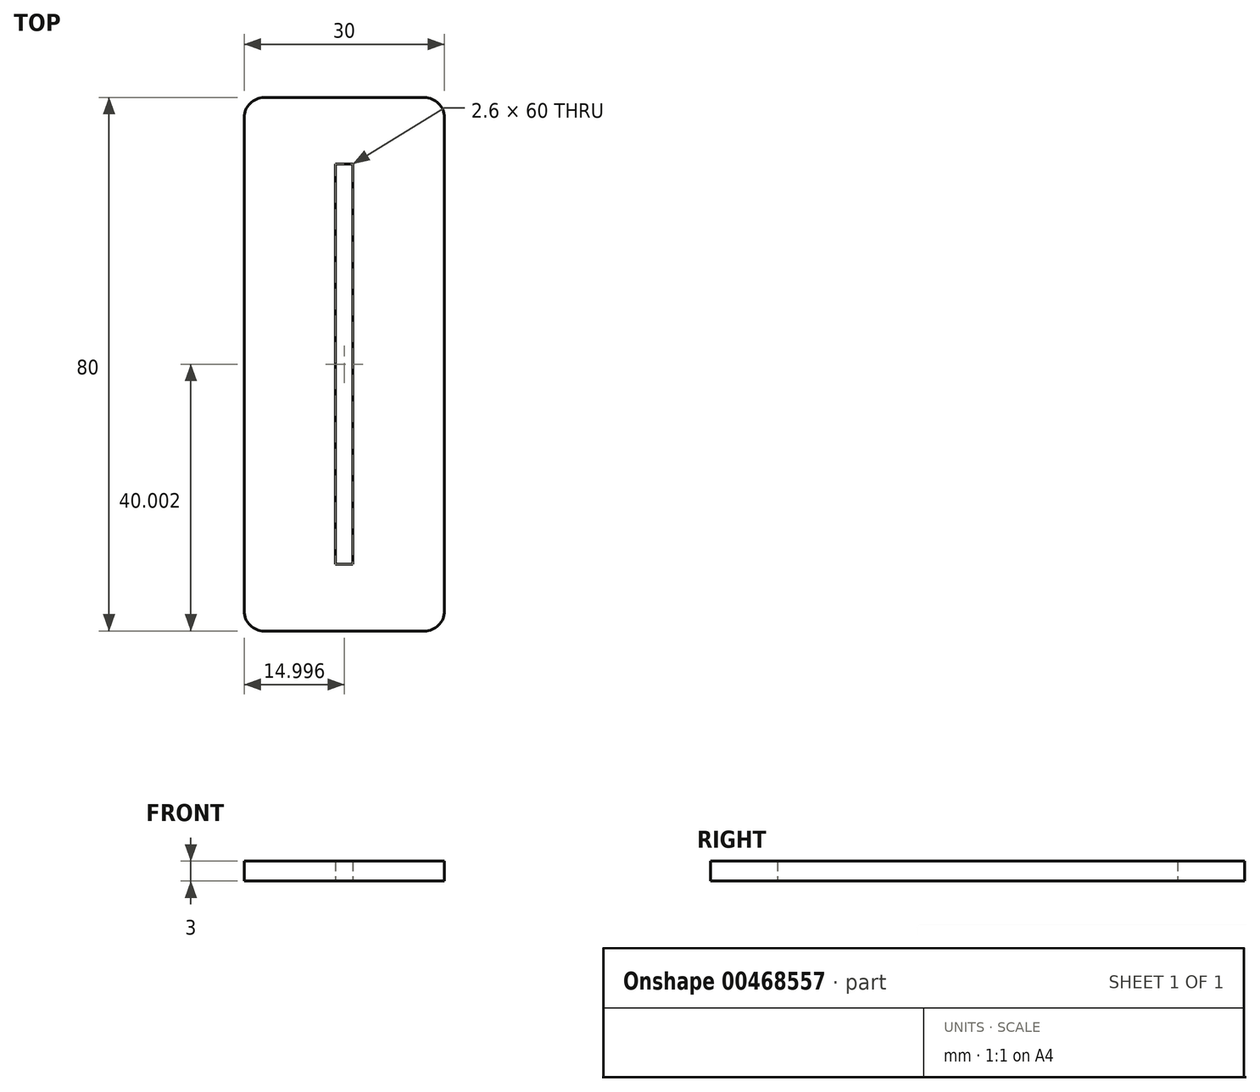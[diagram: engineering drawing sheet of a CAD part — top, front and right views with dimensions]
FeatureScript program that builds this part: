
annotation { "Feature Type Name" : "Feature", "Feature Type Description" : "" }
export const myFeature = defineFeature(function(context is Context, id is Id, definition is map)
    precondition{}
    {
        {
            var Q0;
            Q0=qCreatedBy(makeId("Top.planeOp"),FACE);
            var sketch = newSketch(context, id + "F0", { "sketchPlane" : qUnion([Q0])});
            skLineSegment(sketch, "E0.bottom", {"start": v(-13, 58.78) * mm, "end": v(17, 58.78) * mm});
            skLineSegment(sketch, "E0.top", {"start": v(-13, -21.22) * mm, "end": v(17, -21.22) * mm});
            skLineSegment(sketch, "E0.left", {"start": v(-13, 58.78) * mm, "end": v(-13, -21.22) * mm});
            skLineSegment(sketch, "E0.right", {"start": v(17, 58.78) * mm, "end": v(17, -21.22) * mm});
            skPoint(sketch, "E1", {"position": v(2, 58.78) * mm});
            skLineSegment(sketch, "E2", {"start": v(2, 58.78) * mm, "end": v(2, -21.22) * mm, "construction": true});
            skPoint(sketch, "E3", {"position": v(2, 48.78) * mm});
            skPoint(sketch, "E4", {"position": v(2, -11.22) * mm});
            skLineSegment(sketch, "E5", {"start": v(2, 48.78) * mm, "end": v(0.7, 48.78) * mm});
            skLineSegment(sketch, "E6", {"start": v(0.7, 48.78) * mm, "end": v(0.7, -11.22) * mm});
            skLineSegment(sketch, "E7", {"start": v(0.7, -11.22) * mm, "end": v(2, -11.22) * mm});
            skLineSegment(sketch, "E8", {"start": v(3.3, -11.22) * mm, "end": v(3.3, 48.78) * mm});
            skLineSegment(sketch, "E9", {"start": v(3.3, 48.78) * mm, "end": v(2, 48.78) * mm});
            skLineSegment(sketch, "E10", {"start": v(3.3, -11.22) * mm, "end": v(2, -11.22) * mm});
            skSolve(sketch);
        }
        {
            var Q0;
            Q0=makeQuery(id+"F0.imprint","IMPRINT",FACE,{"disambiguationData":[TD([[makeQuery(id+"F0.imprint","IMPRINT",EDGE,{"derivedFrom":sQuery(id+"F0.wireOp",EDGE,"E0.bottom")}),-1.0]])]});
            extrude(context, id + "F1", {"entities" : qUnion([Q0]), "depth" : 3 * mm, "offsetDistance" : 25 * mm});
        }
        {
            var Q0;
            Q0=makeQuery(id+"F1.opExtrude","SWEPT_EDGE",EDGE,{"disambiguationData":[OSD([sQuery(id+"F0.wireOp",EDGE,"E0.top"),sQuery(id+"F0.wireOp",EDGE,"E0.right")])]});
            var Q1;
            Q1=makeQuery(id+"F1.opExtrude","SWEPT_EDGE",EDGE,{"disambiguationData":[OSD([sQuery(id+"F0.wireOp",EDGE,"E0.top"),sQuery(id+"F0.wireOp",EDGE,"E0.left")])]});
            var Q2;
            Q2=makeQuery(id+"F1.opExtrude","SWEPT_EDGE",EDGE,{"disambiguationData":[OSD([sQuery(id+"F0.wireOp",EDGE,"E0.bottom"),sQuery(id+"F0.wireOp",EDGE,"E0.left")])]});
            var Q3;
            Q3=makeQuery(id+"F1.opExtrude","SWEPT_EDGE",EDGE,{"disambiguationData":[OSD([sQuery(id+"F0.wireOp",EDGE,"E0.bottom"),sQuery(id+"F0.wireOp",EDGE,"E0.right")])]});
            fillet(context, id + "F2", {"entities" : qUnion([Q0, Q1, Q2, Q3]), "radius" : 3 * mm, "tangentPropagation" : true, "allowEdgeOverflow" : false});
        }
    });
